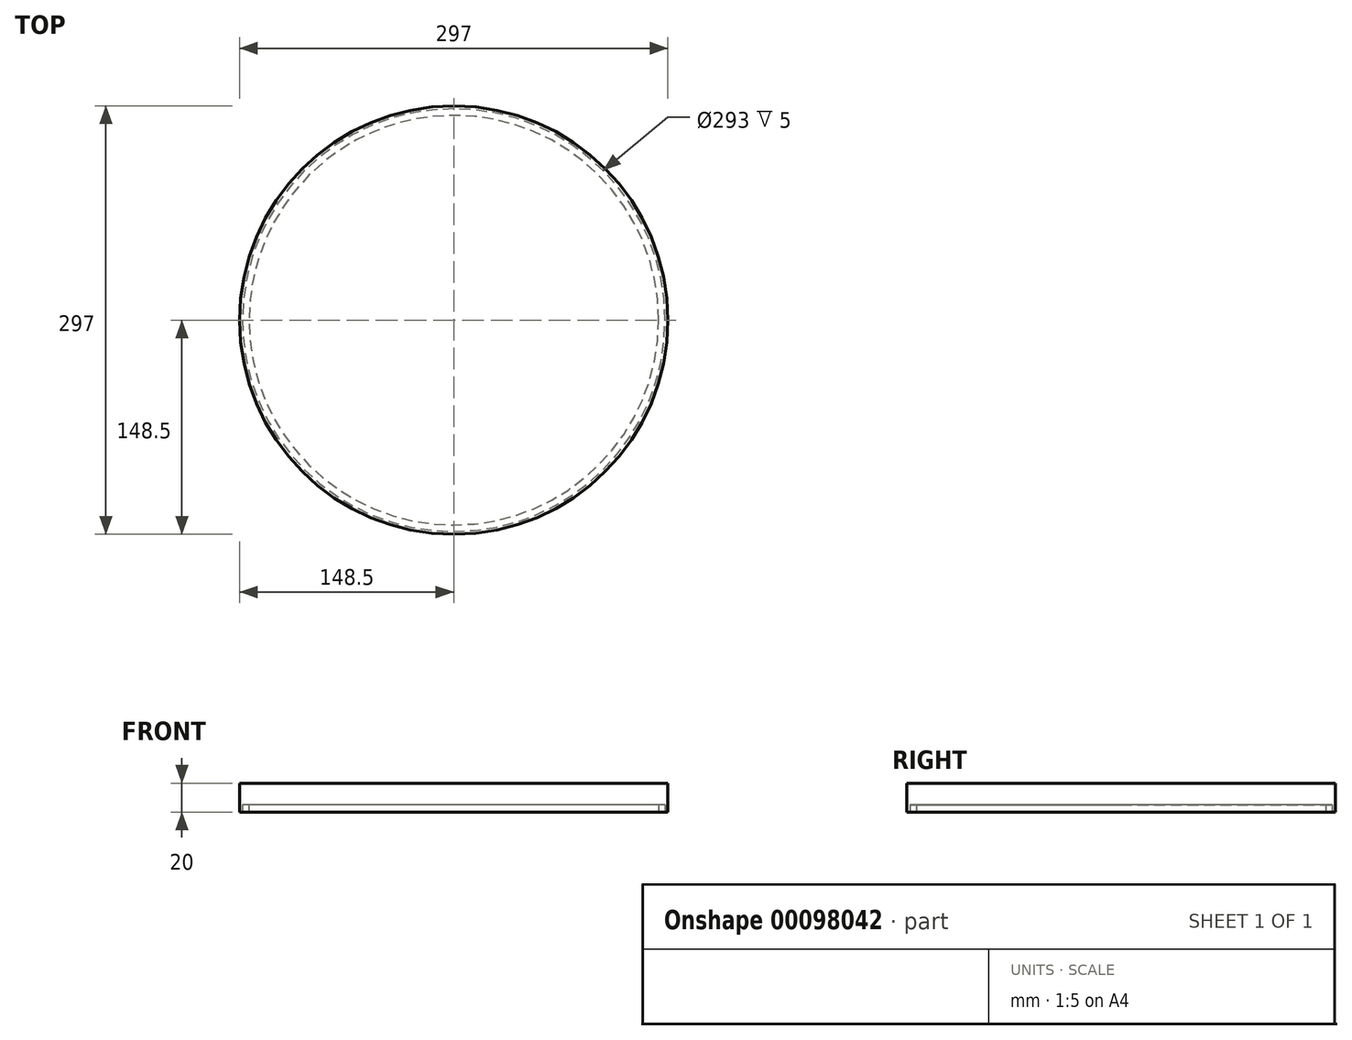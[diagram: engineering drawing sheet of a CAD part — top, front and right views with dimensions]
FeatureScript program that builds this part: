
annotation { "Feature Type Name" : "Feature", "Feature Type Description" : "" }
export const myFeature = defineFeature(function(context is Context, id is Id, definition is map)
    precondition{}
    {
        {
            var Q0;
            Q0=qCreatedBy(makeId("Top.planeOp"),FACE);
            var sketch = newSketch(context, id + "F0", { "sketchPlane" : qUnion([Q0])});
            skCircle(sketch, "E0", {"center": v(0, 0) * mm, "radius": 148.5 * mm});
            skSolve(sketch);
        }
        {
            var Q0;
            Q0=makeQuery(id+"F0.imprint","IMPRINT",FACE,{"disambiguationData":[TD([[makeQuery(id+"F0.imprint","IMPRINT",EDGE,{"derivedFrom":sQuery(id+"F0.wireOp",EDGE,"E0")}),1.0]])]});
            var Q1;
            Q1=makeQuery(id+"F0.imprint","IMPRINT",FACE,{"disambiguationData":[TD([[makeQuery(id+"F0.imprint","IMPRINT",EDGE,{"derivedFrom":sQuery(id+"F0.wireOp",EDGE,"LIXrByum-44Gz-KbWN-PE50-DMeDG7NppI0J")}),1.0]])]});
            var Q2;
            Q2=makeQuery(id+"F0.imprint","IMPRINT",FACE,{"disambiguationData":[TD([[makeQuery(id+"F0.imprint","IMPRINT",EDGE,{"derivedFrom":sQuery(id+"F0.wireOp",EDGE,"oq2Y4278-V4UZ-WgQw-2GIa-DsGsglEtdsp5")}),1.0]])]});
            extrude(context, id + "F1", {"entities" : qUnion([Q0, Q1, Q2]), "depth" : 20 * mm});
        }
        {
            var Q0;
            Q0=makeQuery(id+"F0.imprint","IMPRINT",FACE,{"disambiguationData":[TD([[makeQuery(id+"F0.imprint","IMPRINT",EDGE,{"derivedFrom":sQuery(id+"F0.wireOp",EDGE,"E0")}),1.0]])]});
            var sketch = newSketch(context, id + "F2", { "sketchPlane" : qUnion([Q0])});
            skCircle(sketch, "E1", {"center": v(0, 0) * mm, "radius": 146.5 * mm});
            skCircle(sketch, "E2", {"center": v(0, 0) * mm, "radius": 142 * mm});
            skSolve(sketch);
        }
        {
            var Q0;
            Q0=qSketchRegion(id+"F2",true);
            extrude(context, id + "F3", {"entities" : qUnion([Q0]), "operationType" : NewBodyOperationType.REMOVE, "depth" : 5 * mm});
        }
    });
